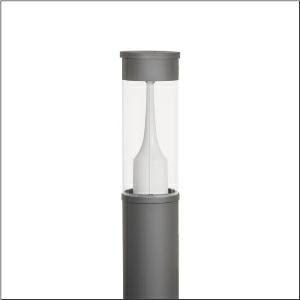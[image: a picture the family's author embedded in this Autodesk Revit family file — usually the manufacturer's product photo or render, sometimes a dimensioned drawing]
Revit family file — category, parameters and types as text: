
# Revit family: city-light_260_iq___st1_2a_5xa5295kf14h_47e0
name_source: partatom
category: Lighting Fixtures
units: mm (PartAtom-declared; Revit-internal decimal feet)

## family parameters
Cut with Voids When Loaded = No
Host = Face
Light Source = No
Part Type = Normal
Room Calculation Point = No
Round Connector Dimension = Use Diameter
Shared = No

## types (1)
- --- (1 x LED, 1540 lm, 10 W, 4000K)
    Apparent Load = 10 VA
    CIE Flux Codes = 22 61 93 96 100
    Color Rendering = 70
    Color Temperature = 4000K
    Default Elevation = 1800 mm
    Description = City-Light 260 iQ, light pillar, Module 540 iQ-SR, primary light control with 3 zone facetted reflector, of plastic, silver coated, highly specular, structured, primary optical cover: cover, of PMMA, transparent, partly coated, light distribution: ST1.2a, primary light characteristic: asymmetric, LED, High Power LED, rated luminous flux: 1.540lm, luminous efficacy: 154lm/W, light colour: 740, colour temperature: 4000K, control gear: ECG iQ, control: presetting dimming logarithmic, Street-Remote, Auto-Match, Temp-Guard, Lumen-Switch, Night-Set, Smart-Wire, Light-Fading, Desk-Remote (wireless, voltage-free reading and setting of iQ features in the workshop via application-optimized NFC function/RFID function), optimised constant luminous flux control (CLO 2.0), with terminal, 6-pole, max. 2.5mm², mains connection: 230..240V, AC, 50/60Hz, start of lifetime: 10W, end of service life: 10W, reduction: 5W, luminaire housing, cylindrical, of extruded aluminium section, coated, Siteco® metallic grey (DB 702S), length: 2.600mm, diameter: 200mm, Module 540 iQ-SR, traffic white (RAL 9016), equipment: standard, protection rating (complete): IP65, insulation class (complete): insulation class II (safety insulation), certification: CE, ENEC, VDE, packaging unit: 1 piece

Light Distribution: ST1.2a
    Height = 500 mm
    Lamp = 1 x LED
    Lamp Light Flux = 1540 lm
    Lamp Power = 10 W
    Lamp count = 1
    Length = 200 mm  [stored 0.656168 ft]
    Luminous efficacy = 154 lm/W
    Manufacturer = Siteco
    ModVariant = No
    Model = 5XA5295KF14H
    Mounting Place = Floor
    Mounting Type = Freestanding
    Number of Poles = 1
    OnlyDefault = Yes
    Power Factor = 1
    Product Name = City-Light 260 iQ | ST1.2a
    Product group = light pillar
    ProductGroupID = 1303
    Protection Class = Protection class II
    Protection Degree = IP 65
    RLX_Detail_Level = 1
    RLX_Emergency_Light_Flux = 0 lm
    RLX_Emergency_Type = 0
    RLX_Emergency_Type_DB = No
    RlxData = <blob elided: 64281 chars, md5=d41a75a1>
    Socket = socket
    Standby Power = 0 W
    System Light Flux = 1540 lm
    System Power = 10 W
    Type Comments = factory setting: luminous flux: 100 % | dim-lin: 254 | 401 mA
    Type Image = l_1006918.jpg
    URL = http://relux.com
    VarID = @adj_109347
    Voltage = 0 V
    Weight = 0.00 kg
    Width = 0 mm  [stored 0 ft]

note: [stored X ft] marks values corroborated as IEEE doubles in the binary element streams (Revit-internal decimal feet)

## geometry (parser evidence)
native form markers: Blend x4, Sweep x9
no freeform markers — native parametric forms only
